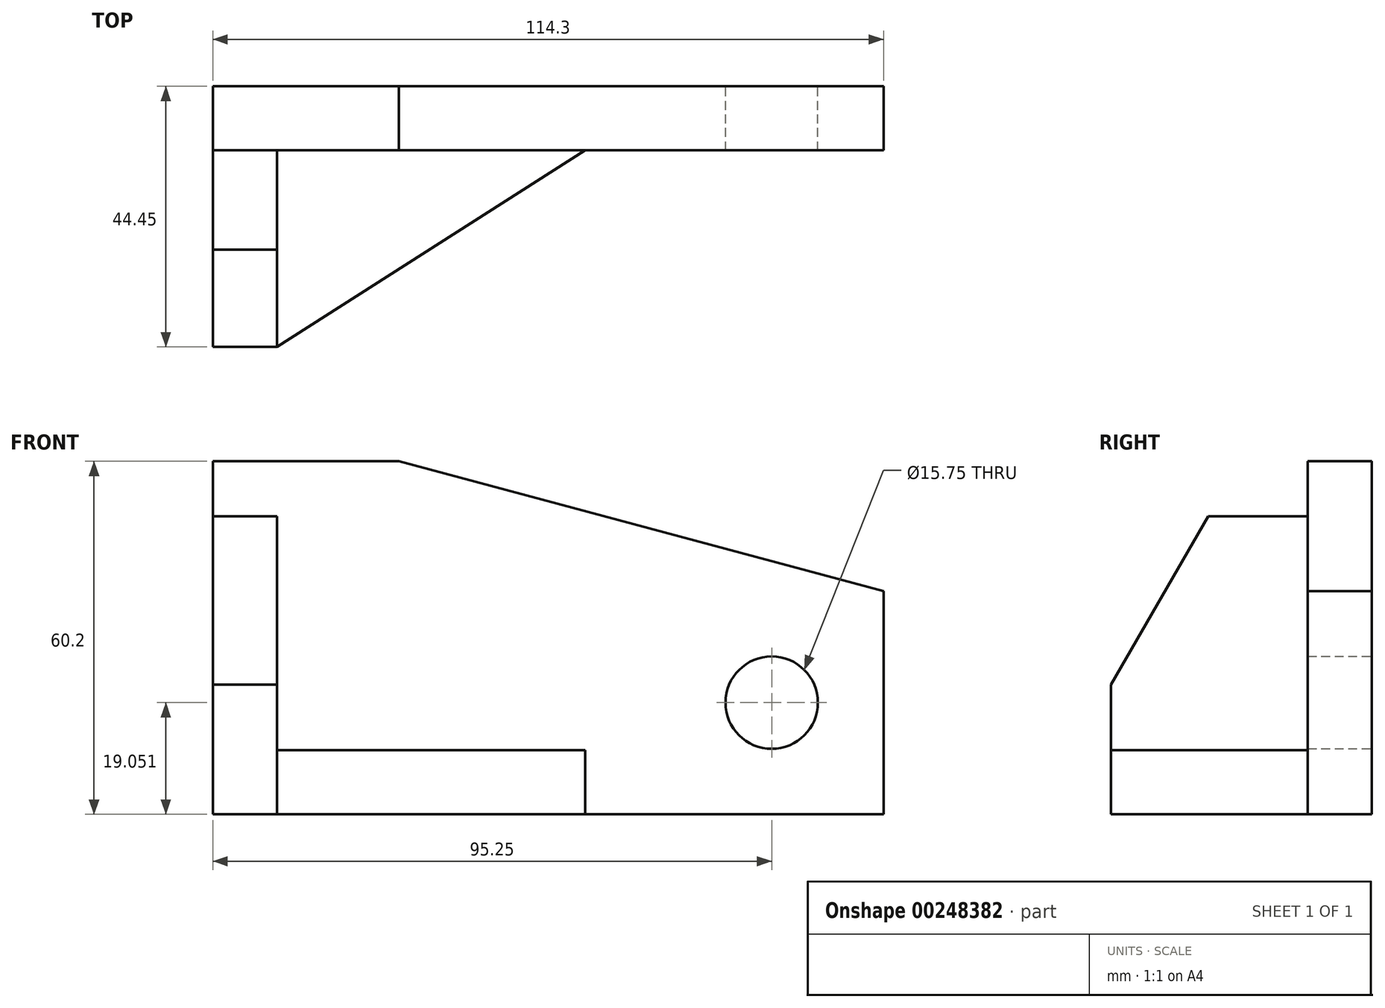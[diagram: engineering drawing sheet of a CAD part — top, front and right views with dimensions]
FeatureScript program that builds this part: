
annotation { "Feature Type Name" : "Feature", "Feature Type Description" : "" }
export const myFeature = defineFeature(function(context is Context, id is Id, definition is map)
    precondition{}
    {
        {
            var Q0;
            Q0=qCreatedBy(makeId("Front.planeOp"),FACE);
            var sketch = newSketch(context, id + "F0", { "sketchPlane" : qUnion([Q0])});
            skLineSegment(sketch, "E0.bottom", {"start": v(0, -30.1) * mm, "end": v(114.3, -30.1) * mm});
            skLineSegment(sketch, "E0.top", {"start": v(0, 30.1) * mm, "end": v(31.75, 30.1) * mm});
            skLineSegment(sketch, "E0.left", {"start": v(0, -30.1) * mm, "end": v(0, 30.1) * mm});
            skLineSegment(sketch, "E0.right", {"start": v(114.3, -30.1) * mm, "end": v(114.3, 7.98) * mm});
            skLineSegment(sketch, "E1", {"start": v(31.75, 30.1) * mm, "end": v(114.3, 7.98) * mm});
            skCircle(sketch, "E2", {"center": v(95.25, -11.05) * mm, "radius": 7.87 * mm});
            skSolve(sketch);
        }
        {
            var Q0;
            Q0=makeQuery(id+"F0.imprint","IMPRINT",FACE,{"disambiguationData":[TD([[makeQuery(id+"F0.imprint","IMPRINT",EDGE,{"derivedFrom":sQuery(id+"F0.wireOp",EDGE,"E0.bottom")}),1.0]])]});
            extrude(context, id + "F1", {"entities" : qUnion([Q0]), "depth" : 10.92 * mm});
        }
        {
            var Q0;
            Q0=makeQuery(id+"F1.opExtrude","SWEPT_FACE",FACE,{"disambiguationData":[OSD([sQuery(id+"F0.wireOp",EDGE,"E0.left")])]});
            var sketch = newSketch(context, id + "F2", { "sketchPlane" : qUnion([Q0])});
            skLineSegment(sketch, "E3.bottom", {"start": v(10.92, -30.1) * mm, "end": v(44.45, -30.1) * mm});
            skLineSegment(sketch, "E3.top", {"start": v(10.92, 20.7) * mm, "end": v(27.88, 20.7) * mm});
            skLineSegment(sketch, "E3.left", {"start": v(10.92, -30.1) * mm, "end": v(10.92, 20.7) * mm});
            skLineSegment(sketch, "E3.right", {"start": v(44.45, -30.1) * mm, "end": v(44.45, -8) * mm});
            skLineSegment(sketch, "E4", {"start": v(27.88, 20.7) * mm, "end": v(44.45, -8) * mm});
            skSolve(sketch);
        }
        {
            var Q0;
            Q0=makeQuery(id+"F2.imprint","IMPRINT",FACE,{"disambiguationData":[TD([[makeQuery(id+"F2.imprint","IMPRINT",EDGE,{"derivedFrom":sQuery(id+"F2.wireOp",EDGE,"E3.bottom")}),1.0]])]});
            extrude(context, id + "F3", {"entities" : qUnion([Q0]), "operationType" : NewBodyOperationType.ADD, "oppositeDirection" : true, "depth" : 10.92 * mm});
        }
        {
            var Q0;
            Q0=makeQuery(id+"F3.boolean.opBoolean","MERGE",FACE,{"derivedFrom":[makeQuery(id+"F1.opExtrude","SWEPT_FACE",FACE,{"disambiguationData":[OSD([sQuery(id+"F0.wireOp",EDGE,"E0.bottom")])]}),makeQuery(id+"F3.opExtrude","SWEPT_FACE",FACE,{"disambiguationData":[OSD([sQuery(id+"F2.wireOp",EDGE,"E3.bottom")])]})]});
            var sketch = newSketch(context, id + "F4", { "sketchPlane" : qUnion([Q0])});
            skLineSegment(sketch, "E5", {"start": v(10.92, 44.45) * mm, "end": v(63.5, 10.92) * mm});
            skSolve(sketch);
        }
        {
            var Q0;
            {var subQ0=sQuery(id+"F4.wireOp",EDGE,"E5");Q0=makeQuery(id+"F4.imprint","IMPRINT",FACE,{"disambiguationData":[TD([[makeQuery(id+"F4.imprint","IMPRINT",EDGE,{"derivedFrom":subQ0}),-1.0]])]});}
            extrude(context, id + "F5", {"entities" : qUnion([Q0]), "operationType" : NewBodyOperationType.ADD, "oppositeDirection" : true, "depth" : 10.92 * mm});
        }
    });
